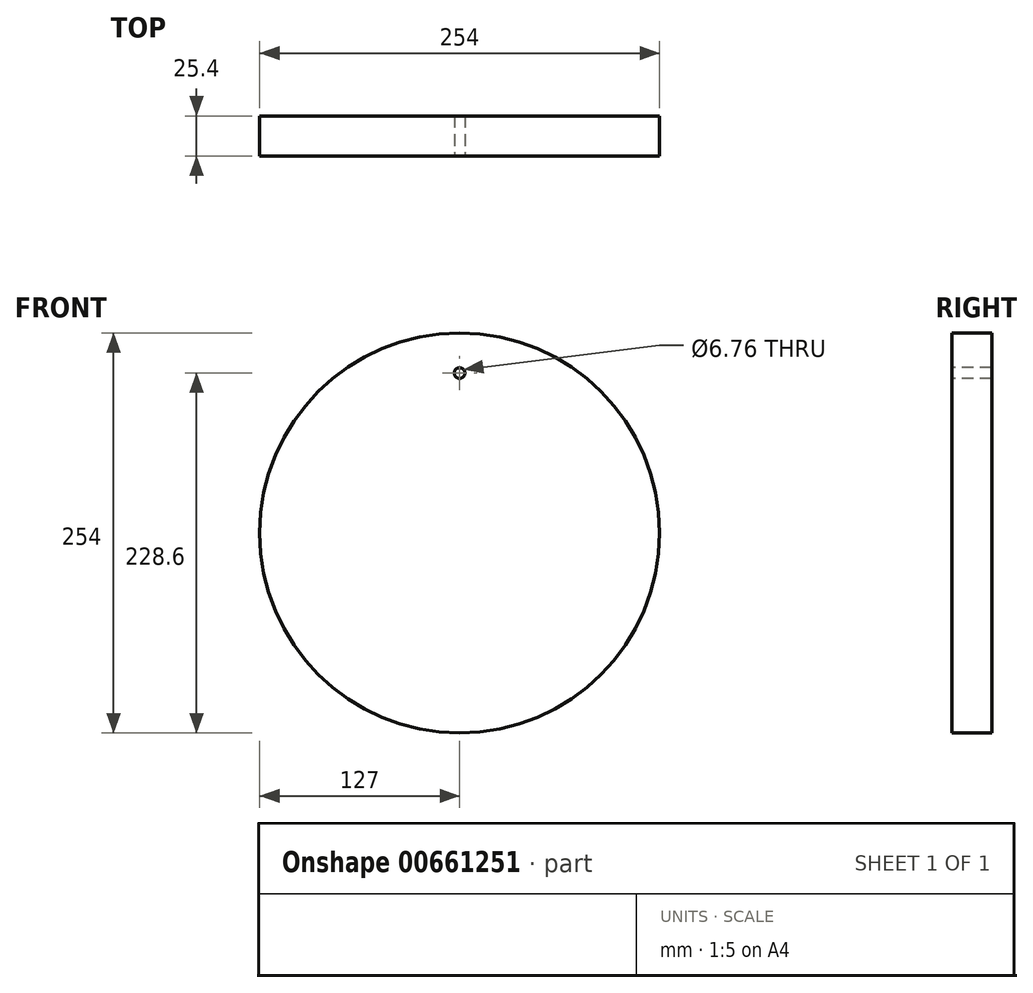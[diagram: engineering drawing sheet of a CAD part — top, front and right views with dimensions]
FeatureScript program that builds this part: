
annotation { "Feature Type Name" : "Feature", "Feature Type Description" : "" }
export const myFeature = defineFeature(function(context is Context, id is Id, definition is map)
    precondition{}
    {
        {
            var Q0;
            Q0=qCreatedBy(makeId("Front.planeOp"),FACE);
            var sketch = newSketch(context, id + "F0", { "sketchPlane" : qUnion([Q0])});
            skCircle(sketch, "E0", {"center": v(0, 0) * mm, "radius": 127 * mm});
            skSolve(sketch);
        }
        {
            var Q0;
            Q0=makeQuery(id+"F0.imprint","IMPRINT",FACE,{"disambiguationData":[TD([[makeQuery(id+"F0.imprint","IMPRINT",EDGE,{"derivedFrom":sQuery(id+"F0.wireOp",EDGE,"E0")}),1.0]])]});
            extrude(context, id + "F1", {"entities" : qUnion([Q0]), "depth" : 25.4 * mm, "offsetDistance" : 25.4 * mm});
        }
        {
            var Q0;
            Q0=makeQuery(id+"F1.opExtrude","CAP_FACE",FACE,{"disambiguationData":[OSD([sQuery(id+"F0.wireOp",EDGE,"E0")])],"isStart":false});
            var sketch = newSketch(context, id + "F2", { "sketchPlane" : qUnion([Q0])});
            skPoint(sketch, "E1", {"position": v(0, 101.6) * mm});
            skSolve(sketch);
        }
        {
            var Q0;
            Q0=sQuery(id+"F2.wireOp",VERTEX,"E1");
            var Q1;
            Q1=makeQuery(id+"F1.opExtrude","SWEPT_BODY",BODY,{"disambiguationData":[OSD([sQuery(id+"F0.wireOp",EDGE,"E0")])]});
            hole(context, id + "F3", {"style" : HoleStyle.SIMPLE, "endStyle" : HoleEndStyle.THROUGH, "standardTappedOrClearance" : lookupTablePath({ "standard" : "ANSI", "fit" : "Normal (ASME)", "size" : "1/4", "type" : "Clearance" }), "standardBlindInLast" : lookupTablePath({ "fit" : "Free", "standard" : "ANSI", "size" : "1/4", "type" : "Clearance" }), "holeDiameter" : 6.76 * mm, "majorDiameter" : 6.35 * mm, "isTappedThrough" : true, "tappedDepth" : 12.7 * mm, "tapClearance" : 3, "locations" : qUnion([Q0]), "scope" : qUnion([Q1])});
        }
    });
